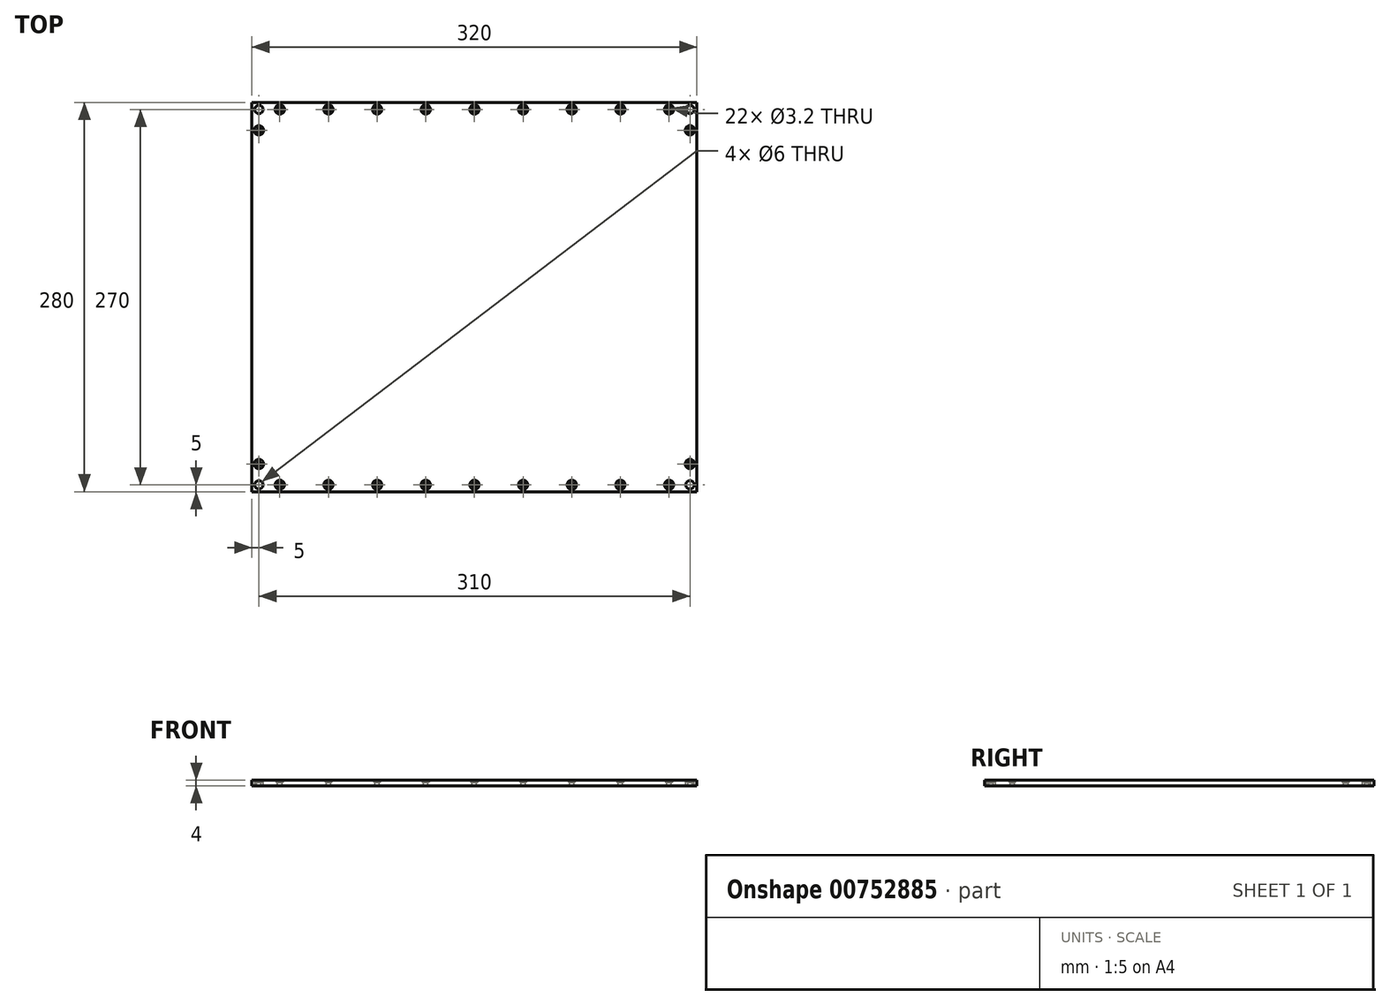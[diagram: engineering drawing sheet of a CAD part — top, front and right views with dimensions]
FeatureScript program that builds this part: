
annotation { "Feature Type Name" : "Feature", "Feature Type Description" : "" }
export const myFeature = defineFeature(function(context is Context, id is Id, definition is map)
    precondition{}
    {
        {
            var Q0;
            Q0=qCreatedBy(makeId("Top.planeOp"),FACE);
            var sketch = newSketch(context, id + "F0", { "sketchPlane" : qUnion([Q0])});
            skLineSegment(sketch, "E0.bottom", {"start": v(-160, 140) * mm, "end": v(160, 140) * mm});
            skLineSegment(sketch, "E0.top", {"start": v(-160, -140) * mm, "end": v(160, -140) * mm});
            skLineSegment(sketch, "E0.left", {"start": v(-160, 140) * mm, "end": v(-160, -140) * mm});
            skLineSegment(sketch, "E0.right", {"start": v(160, 140) * mm, "end": v(160, -140) * mm});
            skPoint(sketch, "E0.middle", {"position": v(0, 0) * mm});
            skLineSegment(sketch, "E1", {"start": v(-160, 0) * mm, "end": v(160, 0) * mm, "construction": true});
            skLineSegment(sketch, "E2.MirrorCS", {"start": v(160, 140) * mm, "end": v(160, 420) * mm});
            skLineSegment(sketch, "E3.0", {"start": v(-155, 135) * mm, "end": v(155, 135) * mm, "construction": true});
            skLineSegment(sketch, "E3.1", {"start": v(-155, 135) * mm, "end": v(-155, -135) * mm, "construction": true});
            skLineSegment(sketch, "E3.2", {"start": v(-155, -135) * mm, "end": v(155, -135) * mm, "construction": true});
            skLineSegment(sketch, "E3.3", {"start": v(155, 135) * mm, "end": v(155, -135) * mm, "construction": true});
            skPoint(sketch, "E4", {"position": v(-155, 135) * mm});
            skPoint(sketch, "E5", {"position": v(155, 135) * mm});
            skPoint(sketch, "E6", {"position": v(155, -135) * mm});
            skPoint(sketch, "E7", {"position": v(-155, -135) * mm});
            skPoint(sketch, "E8", {"position": v(0, -135) * mm});
            skPoint(sketch, "E9", {"position": v(0, 135) * mm});
            skPoint(sketch, "E10.1.0.0", {"position": v(35, 135) * mm});
            skPoint(sketch, "E10.1.0.1", {"position": v(35, -135) * mm});
            skPoint(sketch, "E10.2.0.0", {"position": v(70, 135) * mm});
            skPoint(sketch, "E10.2.0.1", {"position": v(70, -135) * mm});
            skPoint(sketch, "E10.3.0.0", {"position": v(105, 135) * mm});
            skPoint(sketch, "E10.3.0.1", {"position": v(105, -135) * mm});
            skLineSegment(sketch, "E10.direction1", {"start": v(0, 135) * mm, "end": v(35, 135) * mm, "construction": true});
            skPoint(sketch, "E11.1.0.0", {"position": v(-35, 135) * mm});
            skPoint(sketch, "E11.1.0.1", {"position": v(-35, -135) * mm});
            skPoint(sketch, "E11.2.0.0", {"position": v(-70, 135) * mm});
            skPoint(sketch, "E11.2.0.1", {"position": v(-70, -135) * mm});
            skPoint(sketch, "E11.3.0.0", {"position": v(-105, 135) * mm});
            skPoint(sketch, "E11.3.0.1", {"position": v(-105, -135) * mm});
            skLineSegment(sketch, "E11.direction1", {"start": v(0, 135) * mm, "end": v(-35, 135) * mm, "construction": true});
            skPoint(sketch, "E12.0.4.0", {"position": v(140, 135) * mm});
            skPoint(sketch, "E12.1.4.0", {"position": v(140, -135) * mm});
            skLineSegment(sketch, "E13", {"start": v(0, 135) * mm, "end": v(0, -135) * mm, "construction": true});
            skPoint(sketch, "E14.0.4.0", {"position": v(-140, 135) * mm});
            skPoint(sketch, "E14.1.4.0", {"position": v(-140, -135) * mm});
            skPoint(sketch, "E15", {"position": v(-155, 120) * mm});
            skPoint(sketch, "E16.MirrorP", {"position": v(-155, -120) * mm});
            skPoint(sketch, "E17.MirrorP", {"position": v(155, 120) * mm});
            skPoint(sketch, "E18.MirrorP", {"position": v(155, -120) * mm});
            skCircle(sketch, "E19", {"center": v(-155, 135) * mm, "radius": 3 * mm});
            skCircle(sketch, "E20.MirrorC", {"center": v(155, 135) * mm, "radius": 3 * mm});
            skCircle(sketch, "E21.MirrorC", {"center": v(-155, -135) * mm, "radius": 3 * mm});
            skCircle(sketch, "E22.MirrorC", {"center": v(155, -135) * mm, "radius": 3 * mm});
            skSolve(sketch);
        }
        {
            var Q0;
            Q0=makeQuery(id+"F0.imprint","IMPRINT",FACE,{"disambiguationData":[TD([[makeQuery(id+"F0.imprint","IMPRINT",EDGE,{"derivedFrom":sQuery(id+"F0.wireOp",EDGE,"E0.bottom")}),-1.0]])]});
            extrude(context, id + "F1", {"entities" : qUnion([Q0]), "oppositeDirection" : true, "depth" : 4 * mm, "offsetDistance" : 25 * mm});
        }
        {
            var Q0;
            Q0=sQuery(id+"F0.wireOp",VERTEX,"E8");
            var Q1;
            Q1=sQuery(id+"F0.wireOp",VERTEX,"E9");
            var Q2;
            Q2=sQuery(id+"F0.wireOp",VERTEX,"E11.5.0.0");
            var Q3;
            Q3=sQuery(id+"F0.wireOp",VERTEX,"E11.4.0.0");
            var Q4;
            Q4=sQuery(id+"F0.wireOp",VERTEX,"E11.3.0.0");
            var Q5;
            Q5=sQuery(id+"F0.wireOp",VERTEX,"E11.2.0.0");
            var Q6;
            Q6=sQuery(id+"F0.wireOp",VERTEX,"E11.1.0.0");
            var Q7;
            Q7=sQuery(id+"F0.wireOp",VERTEX,"E10.1.0.0");
            var Q8;
            Q8=sQuery(id+"F0.wireOp",VERTEX,"E10.2.0.0");
            var Q9;
            Q9=sQuery(id+"F0.wireOp",VERTEX,"E10.3.0.0");
            var Q10;
            Q10=sQuery(id+"F0.wireOp",VERTEX,"E10.4.0.0");
            var Q11;
            Q11=sQuery(id+"F0.wireOp",VERTEX,"E10.5.0.0");
            var Q12;
            Q12=sQuery(id+"F0.wireOp",VERTEX,"E11.5.0.1");
            var Q13;
            Q13=sQuery(id+"F0.wireOp",VERTEX,"E11.4.0.1");
            var Q14;
            Q14=sQuery(id+"F0.wireOp",VERTEX,"E11.3.0.1");
            var Q15;
            Q15=sQuery(id+"F0.wireOp",VERTEX,"E11.2.0.1");
            var Q16;
            Q16=sQuery(id+"F0.wireOp",VERTEX,"E11.1.0.1");
            var Q17;
            Q17=sQuery(id+"F0.wireOp",VERTEX,"E10.1.0.1");
            var Q18;
            Q18=sQuery(id+"F0.wireOp",VERTEX,"E10.2.0.1");
            var Q19;
            Q19=sQuery(id+"F0.wireOp",VERTEX,"E10.3.0.1");
            var Q20;
            Q20=sQuery(id+"F0.wireOp",VERTEX,"E10.4.0.1");
            var Q21;
            Q21=sQuery(id+"F0.wireOp",VERTEX,"E10.5.0.1");
            var Q22;
            Q22=sQuery(id+"F0.wireOp",VERTEX,"E12.0.4.0");
            var Q23;
            Q23=sQuery(id+"F0.wireOp",VERTEX,"E12.1.4.0");
            var Q24;
            Q24=sQuery(id+"F0.wireOp",VERTEX,"E14.0.4.0");
            var Q25;
            Q25=sQuery(id+"F0.wireOp",VERTEX,"E14.1.4.0");
            var Q26;
            Q26=sQuery(id+"F0.wireOp",VERTEX,"E18.MirrorP");
            var Q27;
            Q27=sQuery(id+"F0.wireOp",VERTEX,"E17.MirrorP");
            var Q28;
            Q28=sQuery(id+"F0.wireOp",VERTEX,"E15");
            var Q29;
            Q29=sQuery(id+"F0.wireOp",VERTEX,"E16.MirrorP");
            var Q30;
            Q30=makeQuery(id+"F1.opExtrude","SWEPT_BODY",BODY,{"disambiguationData":[OSD([sQuery(id+"F0.wireOp",EDGE,"E0.bottom"),sQuery(id+"F0.wireOp",EDGE,"E0.top"),sQuery(id+"F0.wireOp",EDGE,"E0.left"),sQuery(id+"F0.wireOp",EDGE,"E0.right")])]});
            hole(context, id + "F2", {"style" : HoleStyle.C_SINK, "endStyle" : HoleEndStyle.THROUGH, "holeDiameter" : 3.2 * mm, "cSinkDiameter" : 6.72 * mm, "cSinkAngle" : 90 * degree, "majorDiameter" : 3 * mm, "isTappedThrough" : true, "tappedDepth" : 12 * mm, "tapClearance" : 3, "locations" : qUnion([Q0, Q1, Q2, Q3, Q4, Q5, Q6, Q7, Q8, Q9, Q10, Q11, Q12, Q13, Q14, Q15, Q16, Q17, Q18, Q19, Q20, Q21, Q22, Q23, Q24, Q25, Q26, Q27, Q28, Q29]), "scope" : qUnion([Q30])});
        }
    });
